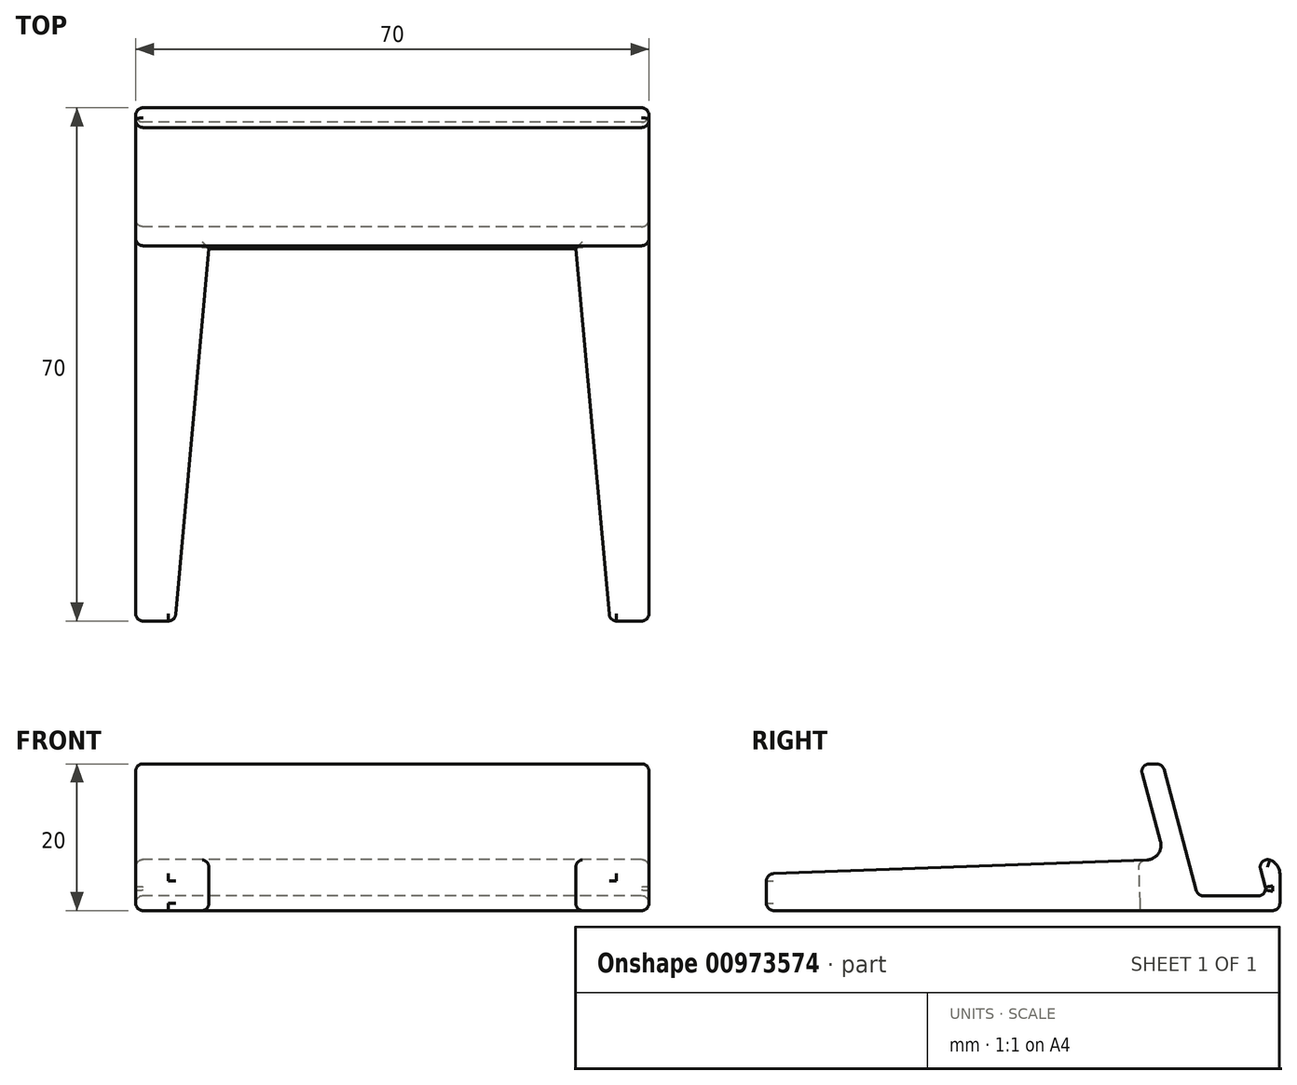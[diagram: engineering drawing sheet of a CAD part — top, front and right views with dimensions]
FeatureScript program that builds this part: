
annotation { "Feature Type Name" : "Feature", "Feature Type Description" : "" }
export const myFeature = defineFeature(function(context is Context, id is Id, definition is map)
    precondition{}
    {
        {
            var Q0;
            Q0=qCreatedBy(makeId("Right.planeOp"),FACE);
            var sketch = newSketch(context, id + "F0", { "sketchPlane" : qUnion([Q0])});
            skLineSegment(sketch, "E0", {"start": v(43.54, 1) * mm, "end": v(43.54, 5) * mm});
            skLineSegment(sketch, "E1", {"start": v(41.54, 7) * mm, "end": v(40.54, 7) * mm});
            skLineSegment(sketch, "E2", {"start": v(40.54, 7) * mm, "end": v(41.54, 3.26) * mm});
            skLineSegment(sketch, "E3", {"start": v(40.58, 2) * mm, "end": v(33.12, 2) * mm});
            skLineSegment(sketch, "E4", {"start": v(32.16, 2.74) * mm, "end": v(27.53, 20) * mm});
            skLineSegment(sketch, "E5", {"start": v(27.53, 20) * mm, "end": v(25.73, 20) * mm});
            skLineSegment(sketch, "E6", {"start": v(24.77, 18.74) * mm, "end": v(27.26, 9.42) * mm});
            skLineSegment(sketch, "E7", {"start": v(25.4, 6.9) * mm, "end": v(-25.5, 5.04) * mm});
            skLineSegment(sketch, "E8", {"start": v(-26.46, 4.04) * mm, "end": v(-26.46, 1) * mm});
            skLineSegment(sketch, "E9", {"start": v(-25.46, 0) * mm, "end": v(42.54, 0) * mm});
            skPoint(sketch, "E10.visualSharp", {"position": v(41.88, 2) * mm});
            skArc(sketch, "E10.filletArc", {"start": v(40.58, 2) * mm, "mid": v(41.37, 2.4) * mm, "end": v(41.54, 3.26) * mm});
            skPoint(sketch, "E11.visualSharp", {"position": v(32.36, 2) * mm});
            skArc(sketch, "E11.filletArc", {"start": v(32.16, 2.74) * mm, "mid": v(32.52, 2.2) * mm, "end": v(33.12, 2) * mm});
            skPoint(sketch, "E12.visualSharp", {"position": v(43.54, 0) * mm});
            skArc(sketch, "E12.filletArc", {"start": v(42.54, 0) * mm, "mid": v(43.25, 0.3) * mm, "end": v(43.54, 1) * mm});
            skPoint(sketch, "E13.visualSharp", {"position": v(43.54, 7) * mm});
            skArc(sketch, "E13.filletArc", {"start": v(43.54, 5) * mm, "mid": v(42.96, 6.41) * mm, "end": v(41.54, 7) * mm});
            skPoint(sketch, "E14.visualSharp", {"position": v(27.91, 7) * mm});
            skArc(sketch, "E14.filletArc", {"start": v(25.4, 6.9) * mm, "mid": v(26.94, 7.72) * mm, "end": v(27.26, 9.42) * mm});
            skPoint(sketch, "E15.visualSharp", {"position": v(24.43, 20) * mm});
            skArc(sketch, "E15.filletArc", {"start": v(25.73, 20) * mm, "mid": v(24.94, 19.6) * mm, "end": v(24.77, 18.74) * mm});
            skPoint(sketch, "E16.visualSharp", {"position": v(-26.46, 5) * mm});
            skArc(sketch, "E16.filletArc", {"start": v(-25.5, 5.04) * mm, "mid": v(-26.18, 4.73) * mm, "end": v(-26.46, 4.04) * mm});
            skPoint(sketch, "E17.visualSharp", {"position": v(-26.46, 0) * mm});
            skArc(sketch, "E17.filletArc", {"start": v(-26.46, 1) * mm, "mid": v(-26.16, 0.3) * mm, "end": v(-25.46, 0) * mm});
            skSolve(sketch);
        }
        {
            var Q0;
            Q0=makeQuery(id+"F0.imprint","IMPRINT",FACE,{"disambiguationData":[TD([[makeQuery(id+"F0.imprint","IMPRINT",EDGE,{"derivedFrom":sQuery(id+"F0.wireOp",EDGE,"E0")}),1.0]])]});
            extrude(context, id + "F1", {"entities" : qUnion([Q0]), "depth" : 70 * mm, "offsetDistance" : 25 * mm});
        }
        {
            var Q0;
            Q0=makeQuery(id+"F1.opExtrude","SWEPT_FACE",FACE,{"disambiguationData":[OSD([sQuery(id+"F0.wireOp",EDGE,"E7")])]});
            var sketch = newSketch(context, id + "F2", { "sketchPlane" : qUnion([Q0])});
            skLineSegment(sketch, "E18", {"start": v(5, -30.5) * mm, "end": v(10, 24.52) * mm});
            skLineSegment(sketch, "E19", {"start": v(10, 24.52) * mm, "end": v(60, 24.52) * mm});
            skLineSegment(sketch, "E20", {"start": v(60, 24.52) * mm, "end": v(65, -30.14) * mm});
            skLineSegment(sketch, "E21", {"start": v(65, -30.14) * mm, "end": v(5, -30.5) * mm});
            skSolve(sketch);
        }
        {
            var Q0;
            {var subQ0=sQuery(id+"F2.wireOp",EDGE,"E19");Q0=makeQuery(id+"F2.imprint","IMPRINT",FACE,{"disambiguationData":[TD([[makeQuery(id+"F2.imprint","IMPRINT",EDGE,{"derivedFrom":subQ0}),-1.0]])]});}
            var Q1;
            {var subQ0=sQuery(id+"F2.wireOp",EDGE,"E21");Q1=makeQuery(id+"F2.imprint","IMPRINT",FACE,{"disambiguationData":[TD([[makeQuery(id+"F2.imprint","IMPRINT",EDGE,{"derivedFrom":subQ0}),-1.0]])]});}
            extrude(context, id + "F3", {"entities" : qUnion([Q0, Q1]), "operationType" : NewBodyOperationType.REMOVE, "oppositeDirection" : true, "depth" : 25 * mm, "offsetDistance" : 25 * mm});
        }
        {
            var Q0;
            Q0=makeQuery(id+"F1.opExtrude","SWEPT_FACE",FACE,{"disambiguationData":[OSD([sQuery(id+"F0.wireOp",EDGE,"E7")])]});
            fillet(context, id + "F4", {"entities" : qUnion([Q0]), "radius" : 1 * mm, "tangentPropagation" : true, "allowEdgeOverflow" : false});
        }
        {
            var Q0;
            Q0=makeQuery(id+"F1.opExtrude","SWEPT_FACE",FACE,{"disambiguationData":[OSD([sQuery(id+"F0.wireOp",EDGE,"E4")])]});
            fillet(context, id + "F5", {"entities" : qUnion([Q0]), "radius" : 1 * mm, "tangentPropagation" : true, "allowEdgeOverflow" : false});
        }
    });
